# Revit family: Skylight_Fakro_FWU-R
name_source: partatom
category: Generic Models
units: mm (PartAtom-declared; Revit-internal decimal feet)

## family parameters
Always vertical = No
Can host rebar = No
Classification Number = 23.30.30.14
Cut with Voids When Loaded = No
Host = Roof
Maintain Annotation Orientation = No
Part Type = Normal
Room Calculation Point = No
Round Connector Dimension = Use Diameter
Shared = No

## types (3) — shared parameters
Assembly Code = B3020110
Hood Length = 601 mm  [stored 1.97178 ft]
Keynote = 08 62 00
Manufacturer = Fakro USA
Manufacturer Fax = 630-543-1011
Manufacturer Website = http://www.fakrousa.com
Model = FWU-R
Product Data = http://www.fakrousa.com
Revision = R1_2016-01
Sales Information = http://www.fakrousa.com
Sash Width = 508 mm  [stored 1.66667 ft]
URL = http://www.fakrousa.com
Unit Width = 597 mm
zero-valued in all types: Cost, Default Elevation, Expected Lifespan (Years), Maintenance Schedule (Months), Warranty Duration (Years)

## per-type parameters (varying)
| type | Description | Sash Length | Unit Height |
| 37x46 | Fakro FWU-R Egress Window - 37x46 | 1085 mm | 1175 mm |
| 24x46 | Fakro FWU-R Egress Window - 24x46 | 1085 mm | 1175 mm |
| 24x38 | Fakro FWU-R Egress Window - 24x38 | 885 mm | 975 mm  [stored 3.19882 ft] |

note: [stored X ft] marks values corroborated as IEEE doubles in the binary element streams (Revit-internal decimal feet)

## geometry (parser evidence)
native form markers: Blend x2, Sweep x3
no freeform markers — native parametric forms only
